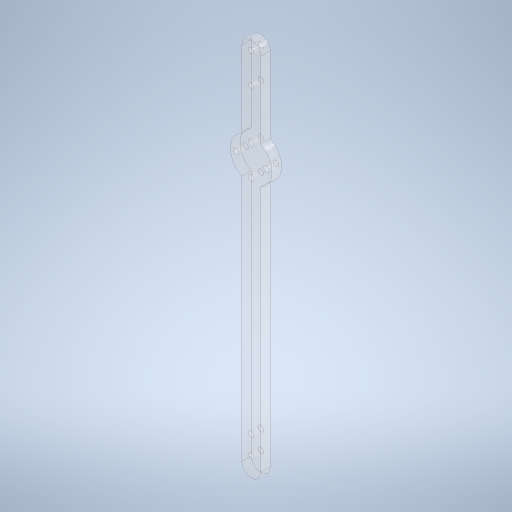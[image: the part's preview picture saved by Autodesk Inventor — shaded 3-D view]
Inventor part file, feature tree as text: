
AUTODESK INVENTOR PART (.ipt)
format: ipt  version: 2023.1 (Build 271208000, 208)  size: 281,088 bytes
history: native  units: mm
features: extrude x1, sketch x1
ambient origin geometry x8: Origin, YZ Plane, XZ Plane, XY Plane, X Axis, Y Axis, Z Axis, Center Point
bodies: Solid1 (feature_tree)
feature tree (2):
  extrude  "Extrusion1"  Depth=10.0mm
  sketch  "Sketch1"  dims[d0=10.0mm d1=10.0mm d2=190.0mm d3=21.0mm d4=50.0mm d5=3.0mm d6=3.0mm d7=3.0mm d8=3.0mm d9=3.0mm d10=8.0mm d11=11.0mm d12=40.0mm d14=360.0deg d16=0.0mm d17=16.0mm d18=5.0mm d19=10.0mm d20=5.0mm d21=0.0mm d22=11.0mm]
